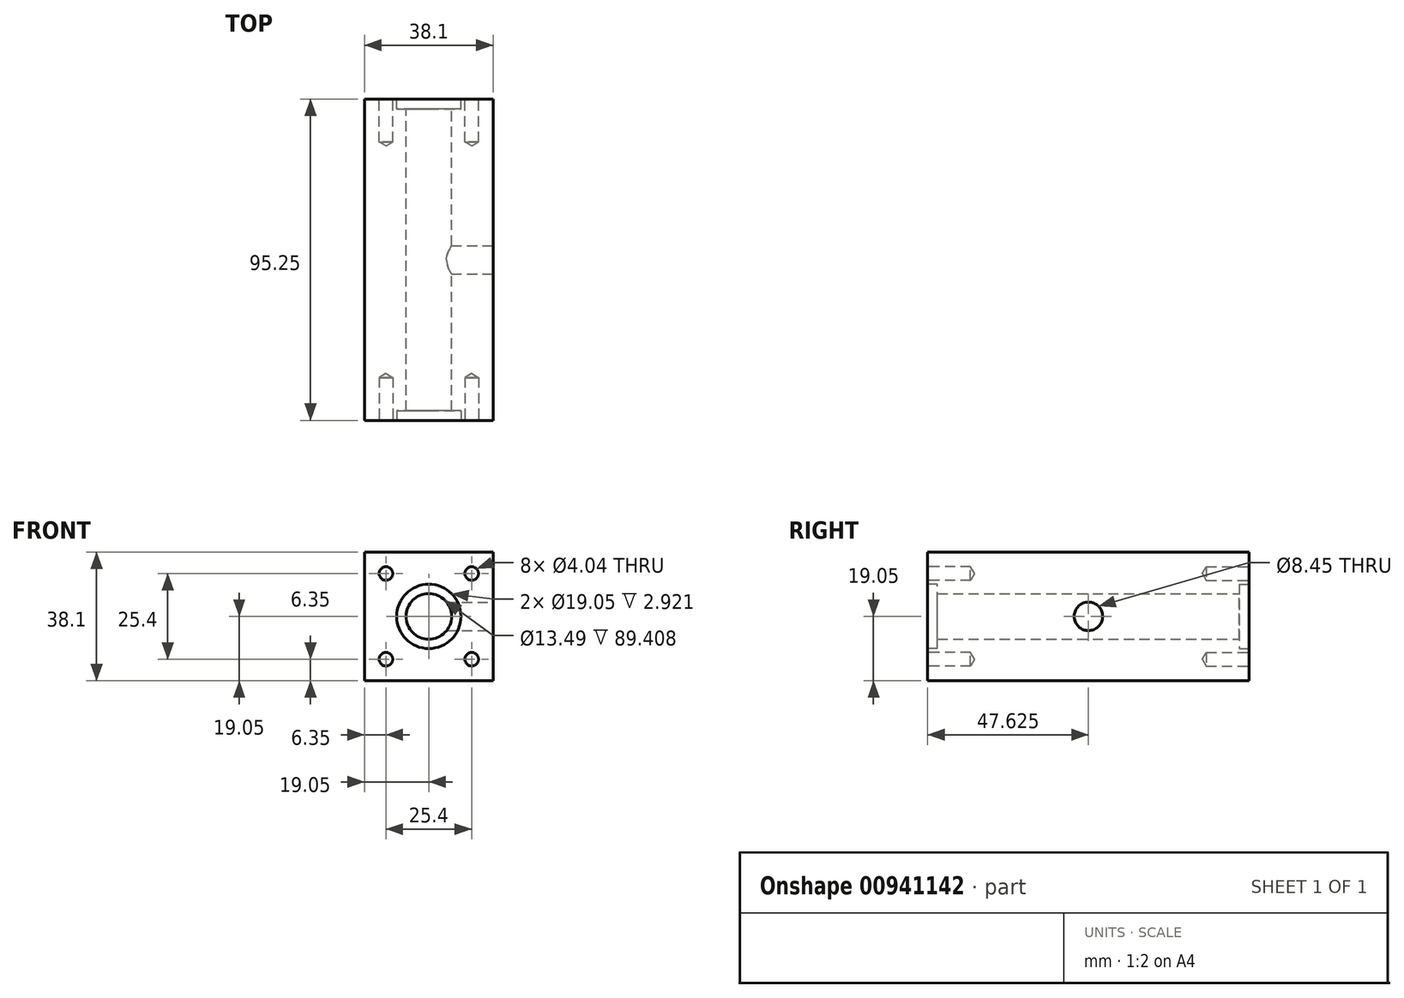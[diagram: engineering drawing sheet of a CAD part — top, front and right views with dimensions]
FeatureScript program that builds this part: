
annotation { "Feature Type Name" : "Feature", "Feature Type Description" : "" }
export const myFeature = defineFeature(function(context is Context, id is Id, definition is map)
    precondition{}
    {
        {
            var Q0;
            Q0=qCreatedBy(makeId("Front.planeOp"),FACE);
            var sketch = newSketch(context, id + "F0", { "sketchPlane" : qUnion([Q0])});
            skLineSegment(sketch, "E0.bottom", {"start": v(-19.05, 19.05) * mm, "end": v(19.05, 19.05) * mm});
            skLineSegment(sketch, "E0.top", {"start": v(-19.05, -19.05) * mm, "end": v(19.05, -19.05) * mm});
            skLineSegment(sketch, "E0.left", {"start": v(-19.05, 19.05) * mm, "end": v(-19.05, -19.05) * mm});
            skLineSegment(sketch, "E0.right", {"start": v(19.05, 19.05) * mm, "end": v(19.05, -19.05) * mm});
            skPoint(sketch, "E0.middle", {"position": v(0, 0) * mm});
            skCircle(sketch, "E1", {"center": v(0, 0) * mm, "radius": 6.75 * mm});
            skSolve(sketch);
        }
        {
            var Q0;
            Q0=makeQuery(id+"F0.imprint","IMPRINT",FACE,{"disambiguationData":[TD([[makeQuery(id+"F0.imprint","IMPRINT",EDGE,{"derivedFrom":sQuery(id+"F0.wireOp",EDGE,"E0.bottom")}),-1.0]])]});
            extrude(context, id + "F1", {"entities" : qUnion([Q0]), "depth" : 95.25 * mm, "offsetDistance" : 25.4 * mm});
        }
        {
            var Q0;
            Q0=makeQuery(id+"F1.opExtrude","CAP_FACE",FACE,{"disambiguationData":[OSD([sQuery(id+"F0.wireOp",EDGE,"E0.bottom"),sQuery(id+"F0.wireOp",EDGE,"E0.top"),sQuery(id+"F0.wireOp",EDGE,"E0.left"),sQuery(id+"F0.wireOp",EDGE,"E0.right"),sQuery(id+"F0.wireOp",EDGE,"E1")])],"isStart":true});
            var sketch = newSketch(context, id + "F2", { "sketchPlane" : qUnion([Q0])});
            skPoint(sketch, "E2", {"position": v(-12.7, -12.7) * mm});
            skPoint(sketch, "E3", {"position": v(-12.7, 12.7) * mm});
            skPoint(sketch, "E4", {"position": v(12.7, 12.7) * mm});
            skPoint(sketch, "E5", {"position": v(12.7, -12.7) * mm});
            skSolve(sketch);
        }
        {
            var Q0;
            Q0=sQuery(id+"F2.wireOp",VERTEX,"E2");
            var Q1;
            Q1=sQuery(id+"F2.wireOp",VERTEX,"E3");
            var Q2;
            Q2=sQuery(id+"F2.wireOp",VERTEX,"E4");
            var Q3;
            Q3=sQuery(id+"F2.wireOp",VERTEX,"E5");
            var Q4;
            Q4=makeQuery(id+"F1.opExtrude","SWEPT_BODY",BODY,{"disambiguationData":[OSD([sQuery(id+"F0.wireOp",EDGE,"E0.bottom"),sQuery(id+"F0.wireOp",EDGE,"E0.top"),sQuery(id+"F0.wireOp",EDGE,"E0.left"),sQuery(id+"F0.wireOp",EDGE,"E0.right"),sQuery(id+"F0.wireOp",EDGE,"E1")])]});
            hole(context, id + "F3", {"style" : HoleStyle.SIMPLE, "endStyle" : HoleEndStyle.BLIND, "standardTappedOrClearance" : lookupTablePath({ "standard" : "ANSI", "engagement" : "75%", "pitch" : "32 tpi", "size" : "#10", "type" : "Tapped" }), "standardBlindInLast" : lookupTablePath({ "standard" : "ANSI", "engagement" : "75%", "pitch" : "32 tpi", "size" : "#10", "type" : "Tapped" }), "holeDiameter" : 4.04 * mm, "showTappedDepth" : true, "holeDepth" : 12.7 * mm, "tappedDepth" : 10.32 * mm, "tapClearance" : 3, "locations" : qUnion([Q0, Q1, Q2, Q3]), "scope" : qUnion([Q4]), "majorDiameter" : 4.83 * mm});
        }
        {
            var Q0;
            Q0=makeQuery(id+"F1.opExtrude","CAP_FACE",FACE,{"disambiguationData":[OSD([sQuery(id+"F0.wireOp",EDGE,"E0.bottom"),sQuery(id+"F0.wireOp",EDGE,"E0.top"),sQuery(id+"F0.wireOp",EDGE,"E0.left"),sQuery(id+"F0.wireOp",EDGE,"E0.right"),sQuery(id+"F0.wireOp",EDGE,"E1")])],"isStart":false});
            var sketch = newSketch(context, id + "F4", { "sketchPlane" : qUnion([Q0])});
            skPoint(sketch, "E6", {"position": v(-12.7, 12.7) * mm});
            skPoint(sketch, "E7", {"position": v(12.7, 12.7) * mm});
            skPoint(sketch, "E8", {"position": v(12.7, -12.7) * mm});
            skPoint(sketch, "E9", {"position": v(-12.7, -12.7) * mm});
            skPoint(sketch, "E10", {"position": v(-19.05, 19.05) * mm});
            skPoint(sketch, "E11", {"position": v(-19.05, -19.05) * mm});
            skPoint(sketch, "E12", {"position": v(19.05, -19.05) * mm});
            skPoint(sketch, "E13", {"position": v(19.05, 19.05) * mm});
            skSolve(sketch);
        }
        {
            var Q0;
            Q0=sQuery(id+"F4.wireOp",VERTEX,"E6");
            var Q1;
            Q1=sQuery(id+"F4.wireOp",VERTEX,"E9");
            var Q2;
            Q2=sQuery(id+"F4.wireOp",VERTEX,"E8");
            var Q3;
            Q3=sQuery(id+"F4.wireOp",VERTEX,"E7");
            var Q4;
            Q4=makeQuery(id+"F1.opExtrude","SWEPT_BODY",BODY,{"disambiguationData":[OSD([sQuery(id+"F0.wireOp",EDGE,"E0.bottom"),sQuery(id+"F0.wireOp",EDGE,"E0.top"),sQuery(id+"F0.wireOp",EDGE,"E0.left"),sQuery(id+"F0.wireOp",EDGE,"E0.right"),sQuery(id+"F0.wireOp",EDGE,"E1")])]});
            hole(context, id + "F5", {"style" : HoleStyle.SIMPLE, "endStyle" : HoleEndStyle.BLIND, "standardTappedOrClearance" : lookupTablePath({ "standard" : "ANSI", "engagement" : "75%", "pitch" : "32 tpi", "size" : "#10", "type" : "Tapped" }), "standardBlindInLast" : lookupTablePath({ "standard" : "ANSI", "engagement" : "75%", "pitch" : "32 tpi", "size" : "#10", "type" : "Tapped" }), "holeDiameter" : 4.04 * mm, "showTappedDepth" : true, "holeDepth" : 12.7 * mm, "tappedDepth" : 10.32 * mm, "tapClearance" : 3, "locations" : qUnion([Q0, Q1, Q2, Q3]), "scope" : qUnion([Q4]), "majorDiameter" : 4.83 * mm});
        }
        {
            var Q0;
            Q0=makeQuery(id+"F1.opExtrude","CAP_FACE",FACE,{"disambiguationData":[OSD([sQuery(id+"F0.wireOp",EDGE,"E0.bottom"),sQuery(id+"F0.wireOp",EDGE,"E0.top"),sQuery(id+"F0.wireOp",EDGE,"E0.left"),sQuery(id+"F0.wireOp",EDGE,"E0.right"),sQuery(id+"F0.wireOp",EDGE,"E1")])],"isStart":false});
            var sketch = newSketch(context, id + "F6", { "sketchPlane" : qUnion([Q0])});
            skCircle(sketch, "E14", {"center": v(0, 0) * mm, "radius": 9.53 * mm});
            skSolve(sketch);
        }
        {
            var Q0;
            Q0=makeQuery(id+"F6.imprint","IMPRINT",FACE,{"disambiguationData":[TD([[makeQuery(id+"F6.imprint","IMPRINT",EDGE,{"derivedFrom":sQuery(id+"F6.wireOp",EDGE,"E14")}),1.0]])]});
            extrude(context, id + "F7", {"entities" : qUnion([Q0]), "operationType" : NewBodyOperationType.REMOVE, "oppositeDirection" : true, "depth" : 2.92 * mm, "offsetDistance" : 25.4 * mm});
        }
        {
            var Q0;
            Q0=makeQuery(id+"F1.opExtrude","CAP_FACE",FACE,{"disambiguationData":[OSD([sQuery(id+"F0.wireOp",EDGE,"E0.bottom"),sQuery(id+"F0.wireOp",EDGE,"E0.top"),sQuery(id+"F0.wireOp",EDGE,"E0.left"),sQuery(id+"F0.wireOp",EDGE,"E0.right"),sQuery(id+"F0.wireOp",EDGE,"E1")])],"isStart":true});
            var sketch = newSketch(context, id + "F8", { "sketchPlane" : qUnion([Q0])});
            skCircle(sketch, "E15", {"center": v(0, 0) * mm, "radius": 9.53 * mm});
            skSolve(sketch);
        }
        {
            var Q0;
            Q0=makeQuery(id+"F8.imprint","IMPRINT",FACE,{"disambiguationData":[TD([[makeQuery(id+"F8.imprint","IMPRINT",EDGE,{"derivedFrom":sQuery(id+"F8.wireOp",EDGE,"E15")}),1.0]])]});
            extrude(context, id + "F9", {"entities" : qUnion([Q0]), "operationType" : NewBodyOperationType.REMOVE, "oppositeDirection" : true, "depth" : 2.92 * mm, "offsetDistance" : 25.4 * mm});
        }
        {
            var Q0;
            Q0=makeQuery(id+"F1.opExtrude","SWEPT_FACE",FACE,{"disambiguationData":[OSD([sQuery(id+"F0.wireOp",EDGE,"E0.right")])]});
            var sketch = newSketch(context, id + "F10", { "sketchPlane" : qUnion([Q0])});
            skPoint(sketch, "E16", {"position": v(-47.63, 0) * mm});
            skSolve(sketch);
        }
        {
            var Q0;
            Q0=sQuery(id+"F10.wireOp",VERTEX,"E16");
            var Q1;
            Q1=makeQuery(id+"F1.opExtrude","SWEPT_BODY",BODY,{"disambiguationData":[OSD([sQuery(id+"F0.wireOp",EDGE,"E0.bottom"),sQuery(id+"F0.wireOp",EDGE,"E0.top"),sQuery(id+"F0.wireOp",EDGE,"E0.left"),sQuery(id+"F0.wireOp",EDGE,"E0.right"),sQuery(id+"F0.wireOp",EDGE,"E1")])]});
            hole(context, id + "F11", {"style" : HoleStyle.SIMPLE, "endStyle" : HoleEndStyle.BLIND, "holeDiameter" : 8.45 * mm, "majorDiameter" : 6.35 * mm, "holeDepth" : 15.88 * mm, "isTappedThrough" : true, "tappedDepth" : 9.98 * mm, "tapClearance" : 3, "locations" : qUnion([Q0]), "scope" : qUnion([Q1])});
        }
    });
